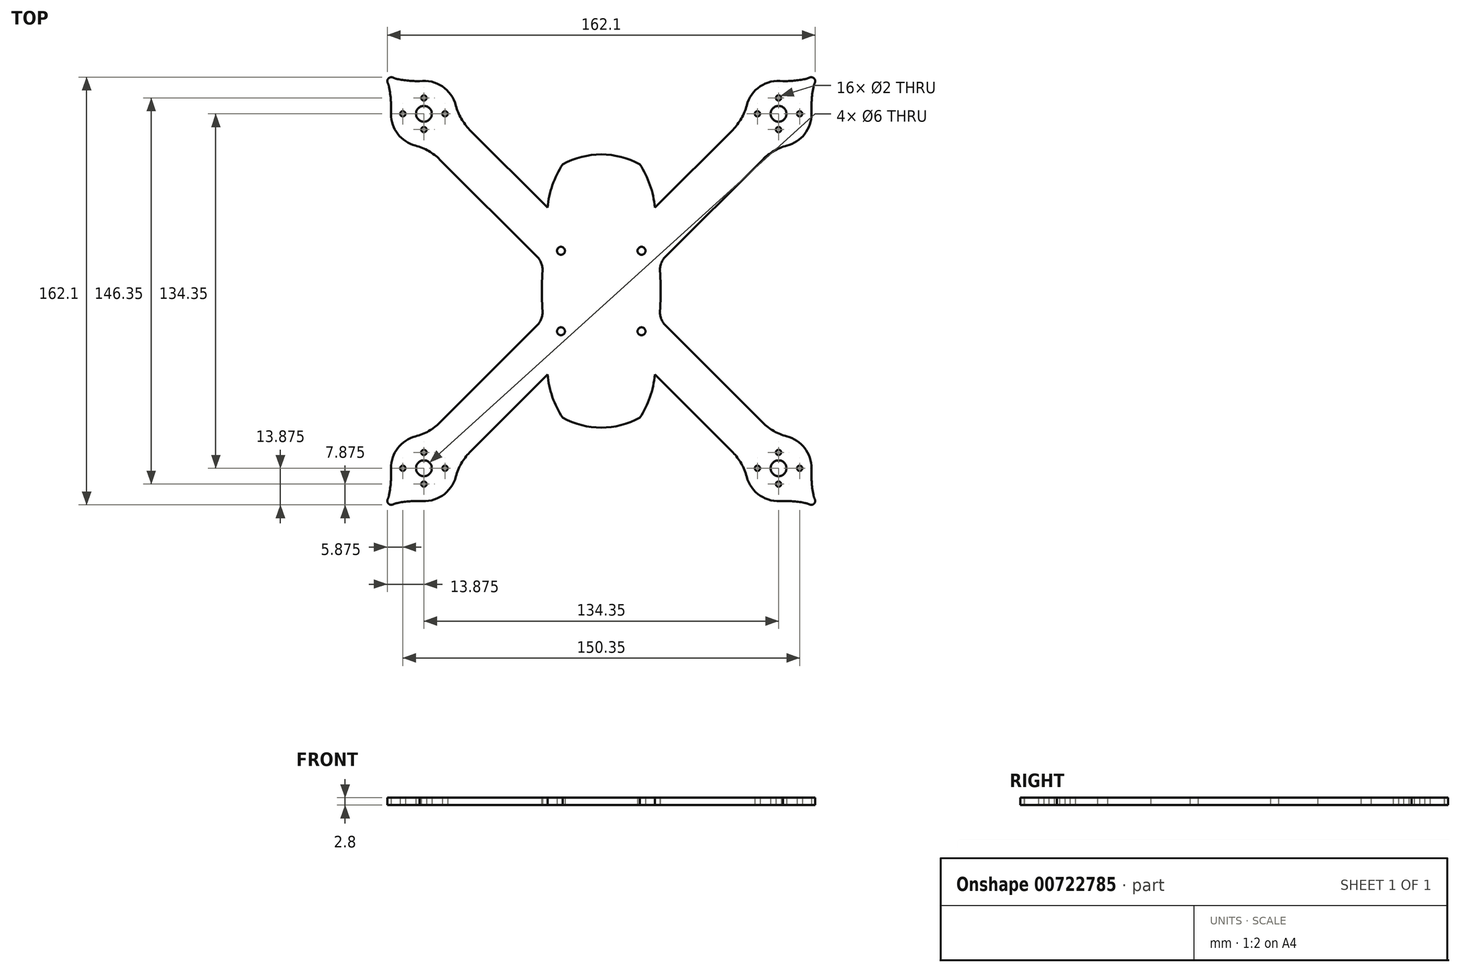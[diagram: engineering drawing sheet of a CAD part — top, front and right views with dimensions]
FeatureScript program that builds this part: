
annotation { "Feature Type Name" : "Feature", "Feature Type Description" : "" }
export const myFeature = defineFeature(function(context is Context, id is Id, definition is map)
    precondition{}
    {
        {
            var Q0;
            Q0=qCreatedBy(makeId("Top.planeOp"),FACE);
            var sketch = newSketch(context, id + "F0", { "sketchPlane" : qUnion([Q0])});
            skCircle(sketch, "E0", {"center": v(0, 0) * mm, "radius": 95 * mm, "construction": true});
            skLineSegment(sketch, "E1", {"start": v(0, -95) * mm, "end": v(0, 95) * mm, "construction": true});
            skLineSegment(sketch, "E2", {"start": v(-95, 0) * mm, "end": v(95, 0) * mm, "construction": true});
            skLineSegment(sketch, "E3", {"start": v(0, 0) * mm, "end": v(67.18, 67.18) * mm, "construction": true});
            skLineSegment(sketch, "E4", {"start": v(0, 0) * mm, "end": v(67.18, -67.18) * mm, "construction": true});
            skCircle(sketch, "E5", {"center": v(67.18, 67.18) * mm, "radius": 51 * mm, "construction": true});
            skCircle(sketch, "E6", {"center": v(67.18, -67.18) * mm, "radius": 51 * mm, "construction": true});
            skCircle(sketch, "E7.MirrorC", {"center": v(-67.18, 67.18) * mm, "radius": 51 * mm, "construction": true});
            skCircle(sketch, "E8.MirrorC", {"center": v(-67.18, -67.18) * mm, "radius": 51 * mm, "construction": true});
            skLineSegment(sketch, "E9.MirrorCS", {"start": v(0, 0) * mm, "end": v(-67.18, 67.18) * mm, "construction": true});
            skLineSegment(sketch, "E10.MirrorCS", {"start": v(0, 0) * mm, "end": v(-67.18, -67.18) * mm, "construction": true});
            skLineSegment(sketch, "E11.bottom", {"start": v(15.25, 15.25) * mm, "end": v(-15.25, 15.25) * mm, "construction": true});
            skLineSegment(sketch, "E11.top", {"start": v(15.25, -15.25) * mm, "end": v(-15.25, -15.25) * mm, "construction": true});
            skLineSegment(sketch, "E11.left", {"start": v(15.25, 15.25) * mm, "end": v(15.25, -15.25) * mm, "construction": true});
            skLineSegment(sketch, "E11.right", {"start": v(-15.25, 15.25) * mm, "end": v(-15.25, -15.25) * mm, "construction": true});
            skCircle(sketch, "E12", {"center": v(-15.25, 15.25) * mm, "radius": 1.5 * mm});
            skCircle(sketch, "E13", {"center": v(15.25, 15.25) * mm, "radius": 1.5 * mm});
            skCircle(sketch, "E14", {"center": v(15.25, -15.25) * mm, "radius": 1.5 * mm});
            skCircle(sketch, "E15", {"center": v(-15.25, -15.25) * mm, "radius": 1.5 * mm});
            skEllipticalArc(sketch, "E16", {});
            skLineSegment(sketch, "E17", {"start": v(76.01, 58.34) * mm, "end": v(58.34, 76.01) * mm, "construction": true});
            skLineSegment(sketch, "E18", {"start": v(67.18, 52.8) * mm, "end": v(67.18, 81.54) * mm, "construction": true});
            skLineSegment(sketch, "E19", {"start": v(43.11, 67.18) * mm, "end": v(71.92, 67.18) * mm, "construction": true});
            skCircle(sketch, "E20", {"center": v(67.18, 67.18) * mm, "radius": 6 * mm, "construction": true});
            skCircle(sketch, "E21", {"center": v(67.18, 67.18) * mm, "radius": 8 * mm, "construction": true});
            skCircle(sketch, "E22", {"center": v(75.18, 67.18) * mm, "radius": 1 * mm});
            skCircle(sketch, "E23", {"center": v(59.18, 67.18) * mm, "radius": 1 * mm});
            skCircle(sketch, "E24", {"center": v(67.18, 73.18) * mm, "radius": 1 * mm});
            skCircle(sketch, "E25", {"center": v(67.18, 61.18) * mm, "radius": 1 * mm});
            skLineSegment(sketch, "E26", {"start": v(49.85, 61.16) * mm, "end": v(18.17, 29.49) * mm});
            skLineSegment(sketch, "E27.MirrorCS", {"start": v(61.16, 49.85) * mm, "end": v(24.28, 12.96) * mm});
            skArc(sketch, "E28", {"start": v(70.3, 55.07) * mm, "mid": v(77.37, 59.94) * mm, "end": v(79.63, 68.21) * mm});
            skPoint(sketch, "E29.visualSharp", {"position": v(66.04, 54.73) * mm});
            skArc(sketch, "E29.filletArc", {"start": v(70.3, 55.07) * mm, "mid": v(65.38, 53.07) * mm, "end": v(61.16, 49.85) * mm});
            skPoint(sketch, "E30.visualSharp", {"position": v(54.73, 66.04) * mm});
            skArc(sketch, "E30.filletArc", {"start": v(49.85, 61.16) * mm, "mid": v(53.07, 65.38) * mm, "end": v(55.07, 70.3) * mm});
            skLineSegment(sketch, "E31", {"start": v(76.02, 76) * mm, "end": v(79.55, 79.55) * mm, "construction": true});
            skLineSegment(sketch, "E32", {"start": v(64.63, 94.39) * mm, "end": v(78.65, 80.45) * mm, "construction": true});
            skArc(sketch, "E33", {"start": v(80.9, 78.9) * mm, "mid": v(80.6, 80.61) * mm, "end": v(78.9, 80.9) * mm});
            skArc(sketch, "E34", {"start": v(80.35, 77.2) * mm, "mid": v(79.7, 72.2) * mm, "end": v(79.68, 67.18) * mm});
            skArc(sketch, "E35.MirrorCS", {"start": v(77.2, 80.33) * mm, "mid": v(72.2, 79.67) * mm, "end": v(67.17, 79.6) * mm});
            skPoint(sketch, "E36.visualSharp", {"position": v(80.61, 78.5) * mm});
            skArc(sketch, "E36.filletArc", {"start": v(80.9, 78.9) * mm, "mid": v(80.57, 78.07) * mm, "end": v(80.35, 77.2) * mm});
            skPoint(sketch, "E37.visualSharp", {"position": v(78.49, 80.6) * mm});
            skArc(sketch, "E37.filletArc", {"start": v(77.2, 80.33) * mm, "mid": v(78.07, 80.56) * mm, "end": v(78.9, 80.9) * mm});
            skArc(sketch, "E38.trimOffspring", {"start": v(68.89, 79.56) * mm, "mid": v(60.22, 77.56) * mm, "end": v(55.07, 70.3) * mm});
            skArc(sketch, "E39.MirrorCS", {"start": v(80.9, -78.9) * mm, "mid": v(80.57, -78.07) * mm, "end": v(80.35, -77.2) * mm});
            skArc(sketch, "E40.MirrorCS", {"start": v(77.2, -80.33) * mm, "mid": v(78.07, -80.56) * mm, "end": v(78.9, -80.9) * mm});
            skArc(sketch, "E41.MirrorCS", {"start": v(80.9, -78.9) * mm, "mid": v(80.6, -80.61) * mm, "end": v(78.9, -80.9) * mm});
            skCircle(sketch, "E42.MirrorC", {"center": v(59.18, -67.18) * mm, "radius": 1 * mm});
            skLineSegment(sketch, "E43.MirrorCS", {"start": v(76.02, -76) * mm, "end": v(79.55, -79.55) * mm, "construction": true});
            skCircle(sketch, "E44.MirrorC", {"center": v(67.18, -61.18) * mm, "radius": 1 * mm});
            skCircle(sketch, "E45.MirrorC", {"center": v(75.18, -67.18) * mm, "radius": 1 * mm});
            skCircle(sketch, "E46.MirrorC", {"center": v(67.18, -73.18) * mm, "radius": 1 * mm});
            skLineSegment(sketch, "E47.MirrorCS", {"start": v(64.63, -94.39) * mm, "end": v(78.65, -80.45) * mm, "construction": true});
            skLineSegment(sketch, "E48.MirrorCS", {"start": v(61.16, -49.85) * mm, "end": v(24.28, -12.96) * mm});
            skArc(sketch, "E49.MirrorCS", {"start": v(80.35, -77.2) * mm, "mid": v(79.7, -72.2) * mm, "end": v(79.68, -67.18) * mm});
            skArc(sketch, "E50.MirrorCS", {"start": v(49.85, -61.16) * mm, "mid": v(53.07, -65.38) * mm, "end": v(55.07, -70.3) * mm});
            skArc(sketch, "E51.MirrorCS", {"start": v(68.89, -79.56) * mm, "mid": v(60.22, -77.56) * mm, "end": v(55.07, -70.3) * mm});
            skLineSegment(sketch, "E52.MirrorCS", {"start": v(67.18, -52.8) * mm, "end": v(67.18, -81.54) * mm, "construction": true});
            skCircle(sketch, "E53.MirrorC", {"center": v(67.18, -67.18) * mm, "radius": 8 * mm, "construction": true});
            skPoint(sketch, "E54.MirrorP", {"position": v(80.61, -78.5) * mm});
            skPoint(sketch, "E55.MirrorP", {"position": v(66.04, -54.73) * mm});
            skArc(sketch, "E56.MirrorCS", {"start": v(70.3, -55.07) * mm, "mid": v(77.37, -59.94) * mm, "end": v(79.63, -68.21) * mm});
            skPoint(sketch, "E57.MirrorP", {"position": v(54.73, -66.04) * mm});
            skCircle(sketch, "E58.MirrorC", {"center": v(67.18, -67.18) * mm, "radius": 6 * mm, "construction": true});
            skLineSegment(sketch, "E59.MirrorCS", {"start": v(43.11, -67.18) * mm, "end": v(71.92, -67.18) * mm, "construction": true});
            skLineSegment(sketch, "E60.MirrorCS", {"start": v(76.01, -58.34) * mm, "end": v(58.34, -76.01) * mm, "construction": true});
            skArc(sketch, "E61.MirrorCS", {"start": v(70.3, -55.07) * mm, "mid": v(65.38, -53.07) * mm, "end": v(61.16, -49.85) * mm});
            skArc(sketch, "E62.MirrorCS", {"start": v(77.2, -80.33) * mm, "mid": v(72.2, -79.67) * mm, "end": v(67.17, -79.6) * mm});
            skPoint(sketch, "E63.MirrorP", {"position": v(78.49, -80.6) * mm});
            skLineSegment(sketch, "E64.MirrorCS", {"start": v(49.85, -61.16) * mm, "end": v(18.17, -29.49) * mm});
            skArc(sketch, "E65.MirrorCS", {"start": v(-77.2, 80.33) * mm, "mid": v(-78.07, 80.56) * mm, "end": v(-78.9, 80.9) * mm});
            skArc(sketch, "E66.MirrorCS", {"start": v(-80.9, 78.9) * mm, "mid": v(-80.57, 78.07) * mm, "end": v(-80.35, 77.2) * mm});
            skArc(sketch, "E67.MirrorCS", {"start": v(-77.2, -80.33) * mm, "mid": v(-78.07, -80.56) * mm, "end": v(-78.9, -80.9) * mm});
            skArc(sketch, "E68.MirrorCS", {"start": v(-80.9, 78.9) * mm, "mid": v(-80.6, 80.61) * mm, "end": v(-78.9, 80.9) * mm});
            skArc(sketch, "E69.MirrorCS", {"start": v(-80.9, -78.9) * mm, "mid": v(-80.6, -80.61) * mm, "end": v(-78.9, -80.9) * mm});
            skArc(sketch, "E70.MirrorCS", {"start": v(-80.9, -78.9) * mm, "mid": v(-80.57, -78.07) * mm, "end": v(-80.35, -77.2) * mm});
            skLineSegment(sketch, "E71.MirrorCS", {"start": v(-76.02, 76) * mm, "end": v(-79.55, 79.55) * mm, "construction": true});
            skCircle(sketch, "E72.MirrorC", {"center": v(-75.18, 67.18) * mm, "radius": 1 * mm});
            skArc(sketch, "E73.MirrorCS", {"start": v(-49.85, 61.16) * mm, "mid": v(-53.07, 65.38) * mm, "end": v(-55.07, 70.3) * mm});
            skCircle(sketch, "E74.MirrorC", {"center": v(-67.18, -73.18) * mm, "radius": 1 * mm});
            skArc(sketch, "E75.MirrorCS", {"start": v(-70.3, 55.07) * mm, "mid": v(-65.38, 53.07) * mm, "end": v(-61.16, 49.85) * mm});
            skCircle(sketch, "E76.MirrorC", {"center": v(-75.18, -67.18) * mm, "radius": 1 * mm});
            skLineSegment(sketch, "E77.MirrorCS", {"start": v(-76.02, -76) * mm, "end": v(-79.55, -79.55) * mm, "construction": true});
            skArc(sketch, "E78.MirrorCS", {"start": v(-80.35, 77.2) * mm, "mid": v(-79.7, 72.2) * mm, "end": v(-79.68, 67.18) * mm});
            skArc(sketch, "E79.MirrorCS", {"start": v(-70.3, 55.07) * mm, "mid": v(-77.37, 59.94) * mm, "end": v(-79.63, 68.21) * mm});
            skCircle(sketch, "E80.MirrorC", {"center": v(-67.18, -61.18) * mm, "radius": 1 * mm});
            skCircle(sketch, "E81.MirrorC", {"center": v(-67.18, 73.18) * mm, "radius": 1 * mm});
            skArc(sketch, "E82.MirrorCS", {"start": v(-70.3, -55.07) * mm, "mid": v(-65.38, -53.07) * mm, "end": v(-61.16, -49.85) * mm});
            skCircle(sketch, "E83.MirrorC", {"center": v(-59.18, -67.18) * mm, "radius": 1 * mm});
            skCircle(sketch, "E84.MirrorC", {"center": v(-59.18, 67.18) * mm, "radius": 1 * mm});
            skArc(sketch, "E85.MirrorCS", {"start": v(-49.85, -61.16) * mm, "mid": v(-53.07, -65.38) * mm, "end": v(-55.07, -70.3) * mm});
            skCircle(sketch, "E86.MirrorC", {"center": v(-67.18, 61.18) * mm, "radius": 1 * mm});
            skLineSegment(sketch, "E87.MirrorCS", {"start": v(-64.63, -94.39) * mm, "end": v(-78.65, -80.45) * mm, "construction": true});
            skArc(sketch, "E88.MirrorCS", {"start": v(-68.89, 79.56) * mm, "mid": v(-60.22, 77.56) * mm, "end": v(-55.07, 70.3) * mm});
            skArc(sketch, "E89.MirrorCS", {"start": v(-70.3, -55.07) * mm, "mid": v(-77.37, -59.94) * mm, "end": v(-79.63, -68.21) * mm});
            skPoint(sketch, "E90.MirrorP", {"position": v(-54.73, 66.04) * mm});
            skCircle(sketch, "E91.MirrorC", {"center": v(-67.18, 67.18) * mm, "radius": 8 * mm, "construction": true});
            skCircle(sketch, "E92.MirrorC", {"center": v(-67.18, -67.18) * mm, "radius": 8 * mm, "construction": true});
            skPoint(sketch, "E93.MirrorP", {"position": v(-54.73, -66.04) * mm});
            skCircle(sketch, "E94.MirrorC", {"center": v(-67.18, 67.18) * mm, "radius": 6 * mm, "construction": true});
            skLineSegment(sketch, "E95.MirrorCS", {"start": v(-67.18, -52.8) * mm, "end": v(-67.18, -81.54) * mm, "construction": true});
            skPoint(sketch, "E96.MirrorP", {"position": v(-66.04, 54.73) * mm});
            skLineSegment(sketch, "E97.MirrorCS", {"start": v(-61.16, 49.85) * mm, "end": v(-24.28, 12.96) * mm});
            skLineSegment(sketch, "E98.MirrorCS", {"start": v(-43.11, 67.18) * mm, "end": v(-71.92, 67.18) * mm, "construction": true});
            skLineSegment(sketch, "E99.MirrorCS", {"start": v(-49.85, -61.16) * mm, "end": v(-18.17, -29.49) * mm});
            skPoint(sketch, "E100.MirrorP", {"position": v(-80.61, 78.5) * mm});
            skArc(sketch, "E101.MirrorCS", {"start": v(-68.89, -79.56) * mm, "mid": v(-60.22, -77.56) * mm, "end": v(-55.07, -70.3) * mm});
            skLineSegment(sketch, "E102.MirrorCS", {"start": v(-67.18, 52.8) * mm, "end": v(-67.18, 81.54) * mm, "construction": true});
            skArc(sketch, "E103.MirrorCS", {"start": v(-77.2, 80.33) * mm, "mid": v(-72.2, 79.67) * mm, "end": v(-67.17, 79.6) * mm});
            skLineSegment(sketch, "E104.MirrorCS", {"start": v(-61.16, -49.85) * mm, "end": v(-24.28, -12.96) * mm});
            skArc(sketch, "E105.MirrorCS", {"start": v(-77.2, -80.33) * mm, "mid": v(-72.2, -79.67) * mm, "end": v(-67.17, -79.6) * mm});
            skPoint(sketch, "E106.MirrorP", {"position": v(-78.49, -80.6) * mm});
            skPoint(sketch, "E107.MirrorP", {"position": v(-80.61, -78.5) * mm});
            skLineSegment(sketch, "E108.MirrorCS", {"start": v(-43.11, -67.18) * mm, "end": v(-71.92, -67.18) * mm, "construction": true});
            skLineSegment(sketch, "E109.MirrorCS", {"start": v(-64.63, 94.39) * mm, "end": v(-78.65, 80.45) * mm, "construction": true});
            skLineSegment(sketch, "E110.MirrorCS", {"start": v(-76.01, -58.34) * mm, "end": v(-58.34, -76.01) * mm, "construction": true});
            skLineSegment(sketch, "E111.MirrorCS", {"start": v(-76.01, 58.34) * mm, "end": v(-58.34, 76.01) * mm, "construction": true});
            skArc(sketch, "E112.MirrorCS", {"start": v(-80.35, -77.2) * mm, "mid": v(-79.7, -72.2) * mm, "end": v(-79.68, -67.18) * mm});
            skLineSegment(sketch, "E113.MirrorCS", {"start": v(-49.85, 61.16) * mm, "end": v(-18.17, 29.49) * mm});
            skPoint(sketch, "E114.MirrorP", {"position": v(-66.04, -54.73) * mm});
            skCircle(sketch, "E115.MirrorC", {"center": v(-67.18, -67.18) * mm, "radius": 6 * mm, "construction": true});
            skPoint(sketch, "E116.MirrorP", {"position": v(-78.49, 80.6) * mm});
            skEllipticalArc(sketch, "E117.trimOffspring", {"construction": true});
            skEllipticalArc(sketch, "E118.trimOffspring", {});
            skEllipticalArc(sketch, "E119.trimOffspring", {"construction": true});
            skPoint(sketch, "E120.visualSharp", {"position": v(-21.98, 10.67) * mm});
            skArc(sketch, "E120.filletArc", {"start": v(-22.24, 7.53) * mm, "mid": v(-22.67, 10.47) * mm, "end": v(-24.28, 12.96) * mm});
            skPoint(sketch, "E121.visualSharp", {"position": v(-21.98, -10.67) * mm});
            skArc(sketch, "E121.filletArc", {"start": v(-24.28, -12.96) * mm, "mid": v(-22.67, -10.47) * mm, "end": v(-22.24, -7.53) * mm});
            skPoint(sketch, "E122.visualSharp", {"position": v(21.98, -10.67) * mm});
            skArc(sketch, "E122.filletArc", {"start": v(22.24, -7.53) * mm, "mid": v(22.67, -10.47) * mm, "end": v(24.28, -12.96) * mm});
            skPoint(sketch, "E123.visualSharp", {"position": v(21.98, 10.67) * mm});
            skArc(sketch, "E123.filletArc", {"start": v(24.28, 12.96) * mm, "mid": v(22.67, 10.47) * mm, "end": v(22.24, 7.53) * mm});
            skArc(sketch, "E124", {"start": v(14.62, 48.03) * mm, "mid": v(16.3, 38.74) * mm, "end": v(18.17, 29.49) * mm, "construction": true});
            skArc(sketch, "E125.MirrorCS", {"start": v(-14.62, 48.03) * mm, "mid": v(-16.3, 38.74) * mm, "end": v(-18.17, 29.49) * mm, "construction": true});
            skArc(sketch, "E126", {"start": v(14.62, 48.03) * mm, "mid": v(0, 51.78) * mm, "end": v(-14.62, 48.03) * mm});
            skArc(sketch, "E127.MirrorCS", {"start": v(14.62, -48.03) * mm, "mid": v(0, -51.78) * mm, "end": v(-14.62, -48.03) * mm});
            skArc(sketch, "E128.MirrorCS", {"start": v(14.62, -48.03) * mm, "mid": v(16.3, -38.74) * mm, "end": v(18.17, -29.49) * mm, "construction": true});
            skArc(sketch, "E129.MirrorCS", {"start": v(-14.62, -48.03) * mm, "mid": v(-16.3, -38.74) * mm, "end": v(-18.17, -29.49) * mm, "construction": true});
            skCircle(sketch, "E130", {"center": v(-67.18, 67.18) * mm, "radius": 3 * mm});
            skCircle(sketch, "E131", {"center": v(67.18, 67.18) * mm, "radius": 3 * mm});
            skCircle(sketch, "E132", {"center": v(67.18, -67.18) * mm, "radius": 3 * mm});
            skCircle(sketch, "E133", {"center": v(-67.18, -67.18) * mm, "radius": 3 * mm});
            skArc(sketch, "E134", {"start": v(-14.62, 48.03) * mm, "mid": v(-18.47, 40.18) * mm, "end": v(-20.32, 31.64) * mm});
            skArc(sketch, "E135.MirrorCS", {"start": v(14.62, 48.03) * mm, "mid": v(18.47, 40.18) * mm, "end": v(20.32, 31.64) * mm});
            skArc(sketch, "E136.MirrorCS", {"start": v(14.62, -48.03) * mm, "mid": v(18.47, -40.18) * mm, "end": v(20.32, -31.64) * mm});
            skArc(sketch, "E137.MirrorCS", {"start": v(-14.62, -48.03) * mm, "mid": v(-18.47, -40.18) * mm, "end": v(-20.32, -31.64) * mm});
            const initialGuessF0  = {"E16": [0, 0, 0, 1, 0.05, 0.0225, 1.419531368990054, 1.722061284599739], "E117.trimOffspring": [0, 0, 0, 1, 0.05, 0.0225, 5.343080262876487, 0.9401050443030987], "E118.trimOffspring": [0, 0, 0, 1, 0.05, 0.0225, 4.561124022579848, 4.8636539381895325], "E119.trimOffspring": [0, 0, 0, 1, 0.05, 0.0225, 2.2014876092866946, 4.081697697892892]};
            skSetInitialGuess(sketch, initialGuessF0);
            skSolve(sketch);
        }
        {
            var Q0;
            {var subQ6=sQuery(id+"F0.wireOp",EDGE,"E65.MirrorCS");Q0=makeQuery(id+"F0.imprint","IMPRINT",FACE,{"disambiguationData":[TD([[makeQuery(id+"F0.imprint","IMPRINT",EDGE,{"derivedFrom":subQ6}),1.0]])]});}
            var Q1;
            Q1=makeQuery(id+"F0.imprint","IMPRINT",FACE,{"disambiguationData":[TD([[makeQuery(id+"F0.imprint","IMPRINT",EDGE,{"derivedFrom":sQuery(id+"F0.wireOp",EDGE,"E12")}),-1.0]])]});
            var Q2;
            Q2=makeQuery(id+"F0.imprint","IMPRINT",FACE,{"disambiguationData":[TD([[makeQuery(id+"F0.imprint","IMPRINT",EDGE,{"derivedFrom":sQuery(id+"F0.wireOp",EDGE,"E22")}),-1.0]])]});
            var Q3;
            {var subQ1=sQuery(id+"F0.wireOp",EDGE,"E39.MirrorCS");Q3=makeQuery(id+"F0.imprint","IMPRINT",FACE,{"disambiguationData":[TD([[makeQuery(id+"F0.imprint","IMPRINT",EDGE,{"derivedFrom":subQ1}),1.0]])]});}
            var Q4;
            {var subQ3=sQuery(id+"F0.wireOp",EDGE,"E67.MirrorCS");Q4=makeQuery(id+"F0.imprint","IMPRINT",FACE,{"disambiguationData":[TD([[makeQuery(id+"F0.imprint","IMPRINT",EDGE,{"derivedFrom":subQ3}),-1.0]])]});}
            var Q5;
            {var subQ0=sQuery(id+"F0.wireOp",EDGE,"E126");var subQ1=sQuery(id+"F0.wireOp",EDGE,"E117.trimOffspring");var subQ2=makeQuery(id+"F0.imprint","INTERSECT",VERTEX,{"disambiguationData":[OD(0.0)],"derivedFrom":[subQ1,subQ0]});Q5=makeQuery(id+"F0.imprint","IMPRINT",FACE,{"disambiguationData":[TD([[makeQuery(id+"F0.imprint","IMPRINT",EDGE,{"disambiguationData":[TD([[subQ2,-1.0]])],"derivedFrom":subQ1}),-1.0]])]});}
            var Q6;
            {var subQ0=sQuery(id+"F0.wireOp",EDGE,"E124");var subQ1=sQuery(id+"F0.wireOp",EDGE,"E117.trimOffspring");var subQ2=makeQuery(id+"F0.imprint","INTERSECT",VERTEX,{"derivedFrom":[subQ1,subQ0]});Q6=makeQuery(id+"F0.imprint","IMPRINT",FACE,{"disambiguationData":[TD([[makeQuery(id+"F0.imprint","IMPRINT",EDGE,{"disambiguationData":[TD([[subQ2,-1.0]])],"derivedFrom":subQ1}),-1.0]])]});}
            extrude(context, id + "F1", {"entities" : qUnion([Q0, Q1, Q2, Q3, Q4, Q5, Q6]), "depth" : 2.8 * mm, "offsetDistance" : 25 * mm});
        }
    });
